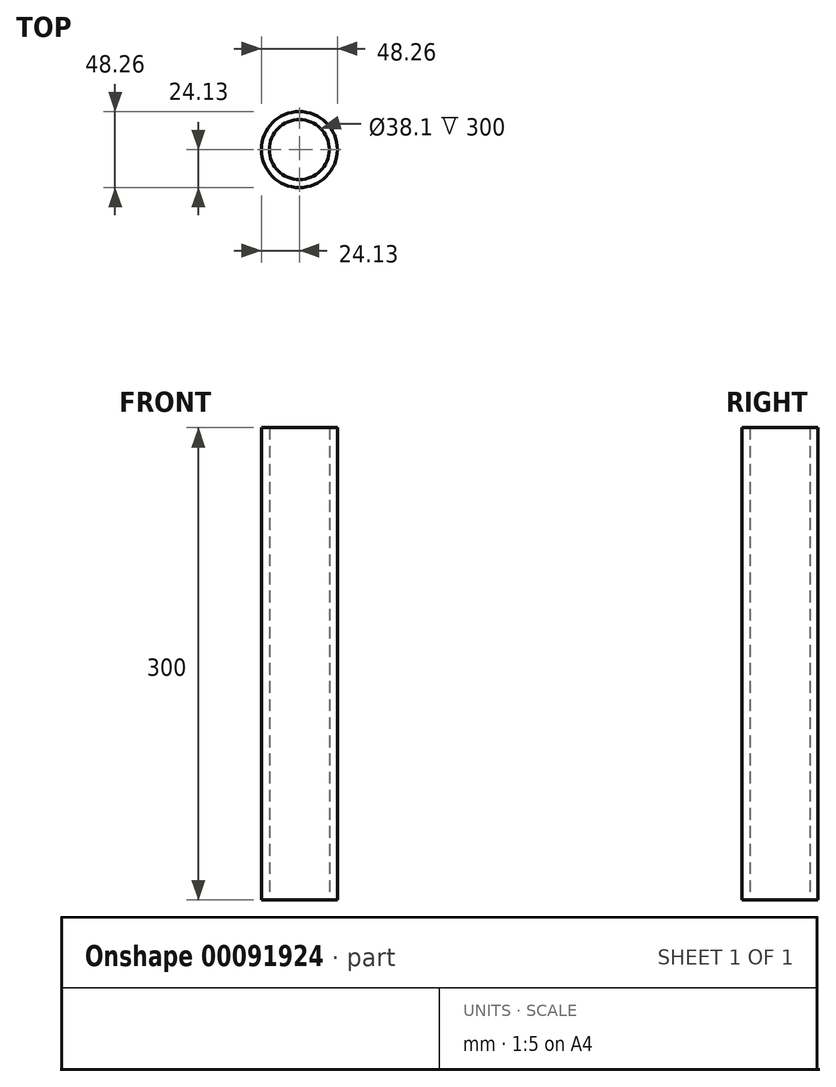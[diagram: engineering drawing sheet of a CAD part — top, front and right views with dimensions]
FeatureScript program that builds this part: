
annotation { "Feature Type Name" : "Feature", "Feature Type Description" : "" }
export const myFeature = defineFeature(function(context is Context, id is Id, definition is map)
    precondition{}
    {
        {
            var Q0;
            Q0=qCreatedBy(makeId("Top.planeOp"),FACE);
            var sketch = newSketch(context, id + "F0", { "sketchPlane" : qUnion([Q0])});
            skCircle(sketch, "E0", {"center": v(0, 0) * mm, "radius": 19.05 * mm});
            skCircle(sketch, "E1", {"center": v(0, 0) * mm, "radius": 24.13 * mm});
            skSolve(sketch);
        }
        {
            var Q0;
            Q0 = qSketchRegion(id + "F0", true);
            extrude(context, id + "F1", {"entities" : qUnion([Q0]), "depth" : 300 * mm});
        }
    });
